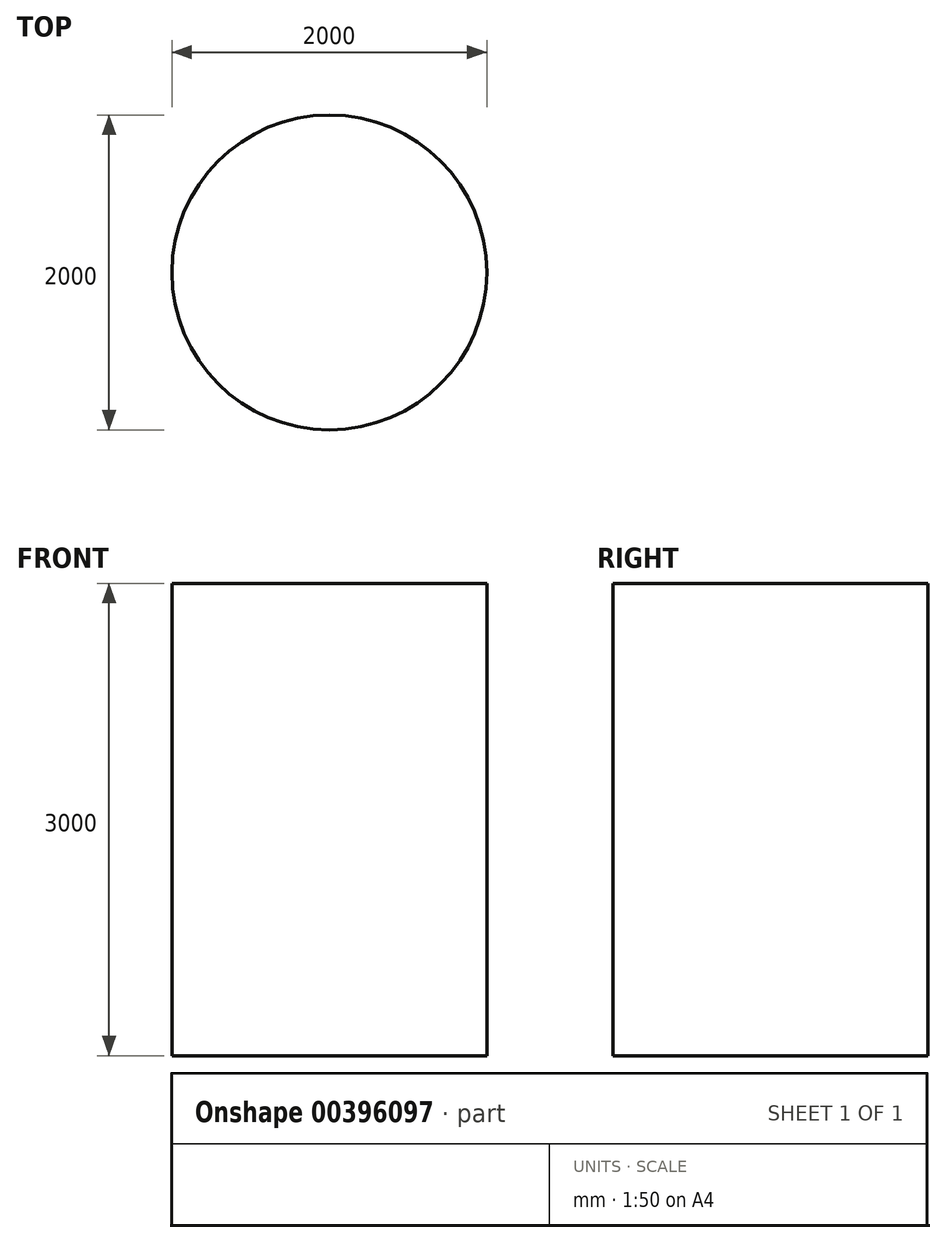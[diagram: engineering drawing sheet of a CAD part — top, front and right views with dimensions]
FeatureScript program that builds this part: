
annotation { "Feature Type Name" : "Feature", "Feature Type Description" : "" }
export const myFeature = defineFeature(function(context is Context, id is Id, definition is map)
    precondition{}
    {
        {
            var Q0;
            Q0=qCreatedBy(makeId("Top.planeOp"),FACE);
            var sketch = newSketch(context, id + "F0", { "sketchPlane" : qUnion([Q0])});
            skCircle(sketch, "E0", {"center": v(0, 0) * mm, "radius": 1000 * mm});
            skSolve(sketch);
        }
        {
            var Q0;
            Q0=makeQuery(id+"F0.imprint","IMPRINT",FACE,{"disambiguationData":[TD([[makeQuery(id+"F0.imprint","IMPRINT",EDGE,{"derivedFrom":sQuery(id+"F0.wireOp",EDGE,"E0")}),1.0]])]});
            extrude(context, id + "F1", {"entities" : qUnion([Q0]), "depth" : 3000 * mm, "offsetDistance" : 25 * mm});
        }
    });
